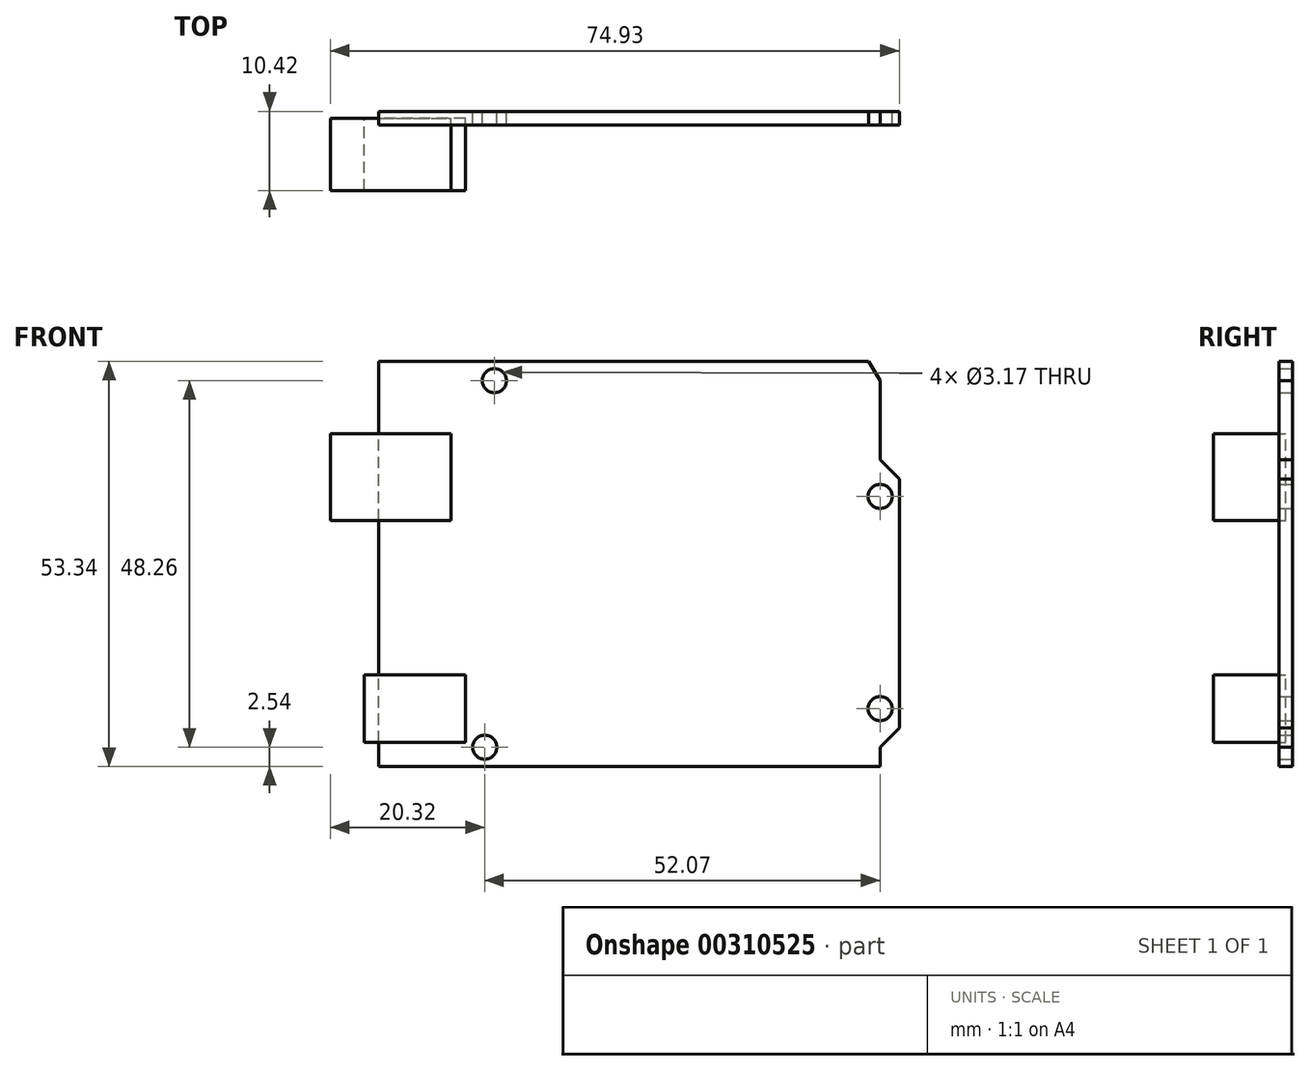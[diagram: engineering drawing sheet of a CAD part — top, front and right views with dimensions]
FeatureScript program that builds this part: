
annotation { "Feature Type Name" : "Feature", "Feature Type Description" : "" }
export const myFeature = defineFeature(function(context is Context, id is Id, definition is map)
    precondition{}
    {
        {
            var Q0;
            Q0=qCreatedBy(makeId("Front.planeOp"),FACE);
            var sketch = newSketch(context, id + "F0", { "sketchPlane" : qUnion([Q0])});
            skLineSegment(sketch, "E0", {"start": v(0, 0) * mm, "end": v(0, 53.34) * mm});
            skLineSegment(sketch, "E1", {"start": v(0, 53.34) * mm, "end": v(64.52, 53.34) * mm});
            skLineSegment(sketch, "E2", {"start": v(0, 0) * mm, "end": v(66.04, 0) * mm});
            skLineSegment(sketch, "E3", {"start": v(66.04, 0) * mm, "end": v(66.04, 2.54) * mm});
            skLineSegment(sketch, "E4", {"start": v(66.04, 50.8) * mm, "end": v(64.52, 53.34) * mm});
            skPoint(sketch, "E5.start.orphan", {"position": v(68.58, 0) * mm});
            skLineSegment(sketch, "E6", {"start": v(66.04, 2.54) * mm, "end": v(68.58, 5.08) * mm});
            skPoint(sketch, "E7.end.orphan", {"position": v(68.58, 2.54) * mm});
            skLineSegment(sketch, "E8", {"start": v(68.58, 5.08) * mm, "end": v(68.58, 37.85) * mm});
            skLineSegment(sketch, "E9", {"start": v(66.04, 40.39) * mm, "end": v(68.58, 37.85) * mm});
            skLineSegment(sketch, "E10.trimOffspring", {"start": v(66.04, 40.39) * mm, "end": v(66.04, 50.8) * mm});
            skSolve(sketch);
        }
        {
            var Q0;
            Q0=qCreatedBy(makeId("Front.planeOp"),FACE);
            var sketch = newSketch(context, id + "F1", { "sketchPlane" : qUnion([Q0])});
            skLineSegment(sketch, "E11", {"start": v(0, 0) * mm, "end": v(0, 3.18) * mm});
            skLineSegment(sketch, "E12", {"start": v(0, 3.18) * mm, "end": v(-1.9, 3.18) * mm});
            skLineSegment(sketch, "E13", {"start": v(0, 12.07) * mm, "end": v(-1.9, 12.07) * mm});
            skLineSegment(sketch, "E14", {"start": v(-1.9, 3.17) * mm, "end": v(-1.9, 12.07) * mm});
            skLineSegment(sketch, "E15", {"start": v(0, 3.18) * mm, "end": v(11.43, 3.18) * mm});
            skLineSegment(sketch, "E16", {"start": v(11.43, 3.17) * mm, "end": v(11.43, 12.07) * mm});
            skLineSegment(sketch, "E17", {"start": v(11.43, 12.07) * mm, "end": v(0, 12.07) * mm});
            skLineSegment(sketch, "E18", {"start": v(-6.35, 0) * mm, "end": v(-6.35, 32.39) * mm});
            skLineSegment(sketch, "E19", {"start": v(-6.35, 32.39) * mm, "end": v(-6.35, 43.82) * mm});
            skLineSegment(sketch, "E20", {"start": v(-6.35, 32.39) * mm, "end": v(0, 32.39) * mm});
            skLineSegment(sketch, "E21", {"start": v(0, 32.39) * mm, "end": v(9.53, 32.39) * mm});
            skLineSegment(sketch, "E22", {"start": v(-6.35, 43.82) * mm, "end": v(9.52, 43.82) * mm});
            skLineSegment(sketch, "E23", {"start": v(9.52, 43.82) * mm, "end": v(9.53, 32.39) * mm});
            skPoint(sketch, "E24.start.orphan", {"position": v(0, 49.34) * mm});
            skSolve(sketch);
        }
        {
            var Q0;
            Q0=makeQuery(id+"F0.imprint","IMPRINT",FACE,{"disambiguationData":[TD([[makeQuery(id+"F0.imprint","IMPRINT",EDGE,{"derivedFrom":sQuery(id+"F0.wireOp",EDGE,"E0")}),-1.0]])]});
            var sketch = newSketch(context, id + "F2", { "sketchPlane" : qUnion([Q0])});
            skPoint(sketch, "E25.start.orphan", {"position": v(0, 123.58) * mm});
            skCircle(sketch, "E26", {"center": v(15.24, 50.8) * mm, "radius": 1.59 * mm});
            skPoint(sketch, "E27.orphan", {"position": v(15.24, 0) * mm});
            skPoint(sketch, "E28.orphan", {"position": v(0, 50.8) * mm});
            skCircle(sketch, "E29", {"center": v(13.97, 2.54) * mm, "radius": 1.59 * mm});
            skPoint(sketch, "E30.orphan", {"position": v(13.97, 0) * mm});
            skPoint(sketch, "E31.start.orphan", {"position": v(0, 2.54) * mm});
            skCircle(sketch, "E32", {"center": v(66.04, 7.62) * mm, "radius": 1.59 * mm});
            skPoint(sketch, "E33.orphan", {"position": v(0, 7.62) * mm});
            skPoint(sketch, "E34.orphan", {"position": v(66.04, 0) * mm});
            skLineSegment(sketch, "E35", {"start": v(66.04, 6.03) * mm, "end": v(66.04, 9.2) * mm});
            skCircle(sketch, "E36", {"center": v(66.04, 35.56) * mm, "radius": 1.59 * mm});
            skPoint(sketch, "E37.orphan", {"position": v(0, 35.56) * mm});
            skSolve(sketch);
        }
        {
            var Q0;
            Q0=makeQuery(id+"F0.imprint","IMPRINT",FACE,{"disambiguationData":[TD([[makeQuery(id+"F0.imprint","IMPRINT",EDGE,{"derivedFrom":sQuery(id+"F0.wireOp",EDGE,"E0")}),-1.0]])]});
            extrude(context, id + "F3", {"entities" : qUnion([Q0]), "endBound" : BoundingType.SYMMETRIC, "depth" : 1.78 * mm});
        }
        {
            var Q0;
            Q0=qSketchRegion(id+"F1",true);
            extrude(context, id + "F4", {"entities" : qUnion([Q0]), "depth" : 9.52 * mm});
        }
        {
            var Q0;
            Q0=qSketchRegion(id+"F2",true);
            extrude(context, id + "F5", {"entities" : qUnion([Q0]), "operationType" : NewBodyOperationType.REMOVE, "endBound" : BoundingType.SYMMETRIC, "depth" : 25.4 * mm});
        }
    });
